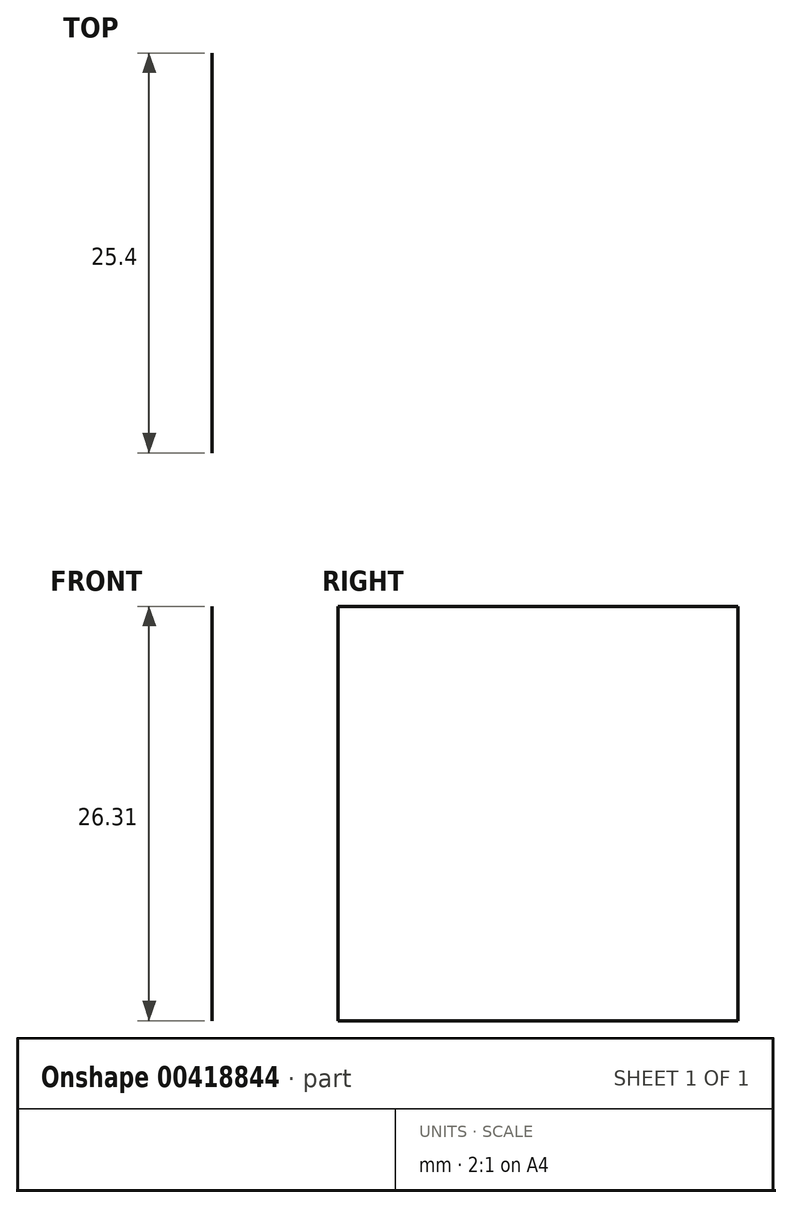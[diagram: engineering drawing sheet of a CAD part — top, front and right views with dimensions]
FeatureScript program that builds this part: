
annotation { "Feature Type Name" : "Feature", "Feature Type Description" : "" }
export const myFeature = defineFeature(function(context is Context, id is Id, definition is map)
    precondition{}
    {
        {
            var Q0;
            Q0=qCreatedBy(makeId("Front.planeOp"),FACE);
            var sketch = newSketch(context, id + "F0", { "sketchPlane" : qUnion([Q0])});
            skLineSegment(sketch, "E0.bottom", {"start": v(0, 0) * mm, "end": v(-50.8, 0) * mm});
            skLineSegment(sketch, "E0.top", {"start": v(0, 26.31) * mm, "end": v(-50.8, 26.31) * mm});
            skLineSegment(sketch, "E0.left", {"start": v(0, 0) * mm, "end": v(0, 26.31) * mm});
            skLineSegment(sketch, "E0.right", {"start": v(-50.8, 0) * mm, "end": v(-50.8, 26.31) * mm});
            skSolve(sketch);
        }
        {
            var Q0;
            Q0=sQuery(id+"F0.wireOp",EDGE,"E0.right");
            extrude(context, id + "F1", {"bodyType" : ToolBodyType.SURFACE, "surfaceEntities" : qUnion([Q0]), "depth" : 25.4 * mm});
        }
    });
